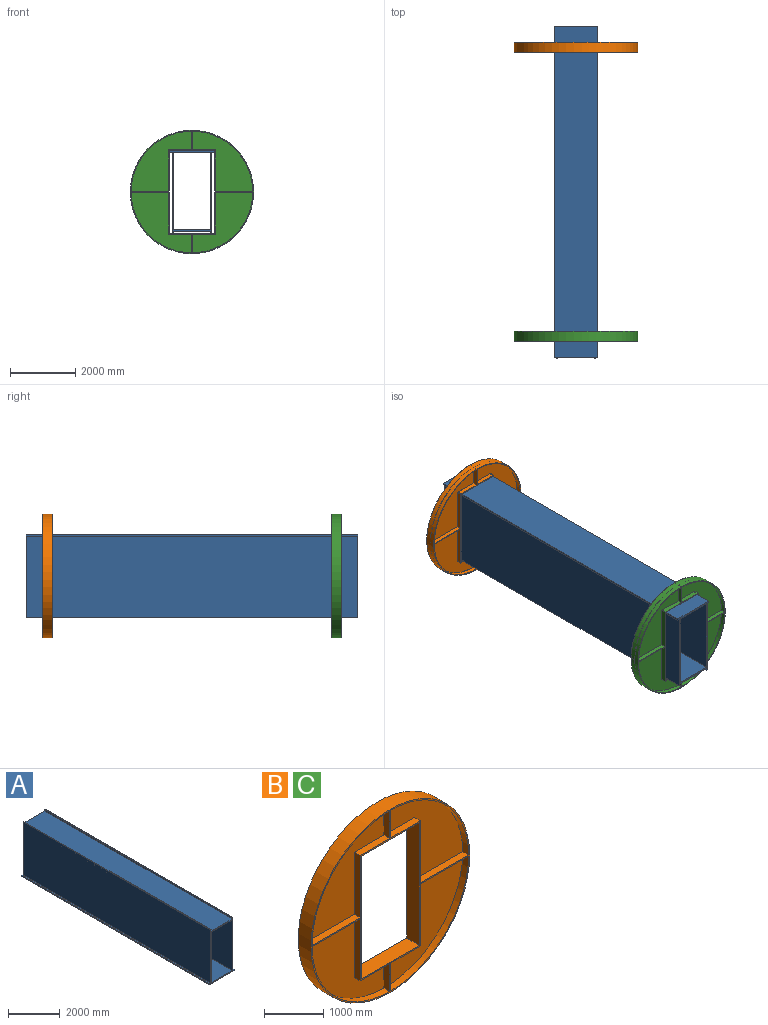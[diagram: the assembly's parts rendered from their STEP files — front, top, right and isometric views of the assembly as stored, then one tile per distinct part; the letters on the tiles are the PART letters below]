
ASSEMBLY  parts=3 mates=2
PART A: 18 faces, bbox 1346.2x10207.6x2552.7 mm
  f0: plane 10207.63x63.5mm, normal (0,0,1), area 648184.2mm2, adj f1,f15,f16,f17
  f1: plane 10207.63x2501.9mm, normal (1,0,0), area 25538457mm2, adj f0,f2,f16,f17
  f2: plane 10207.63x38.1mm, normal (0,0,1), area 388910.5mm2, adj f1,f3,f16,f17
  f3: plane 10207.63x63.5mm, normal (-1,0,0), area 648184.2mm2, adj f2,f4,f16,f17
  f4: plane 10207.63x1143mm, normal (0,0,1), area 11667315.4mm2, adj f3,f5,f16,f17
  f5: plane 10207.63x63.5mm, normal (1,0,0), area 648184.2mm2, adj f4,f6,f16,f17
  f6: plane 10207.63x38.1mm, normal (0,0,1), area 388910.5mm2, adj f5,f7,f16,f17
  f7: plane 10207.63x2501.9mm, normal (-1,0,0), area 25538457mm2, adj f6,f8,f16,f17
  f8: plane 10207.63x63.5mm, normal (0,0,1), area 648184.2mm2, adj f7,f9,f16,f17
  f9: plane 10207.63x50.8mm, normal (-1,0,0), area 518547.3mm2, adj f8,f10,f16,f17
  f10: plane 10207.63x1346.2mm, normal (0,0,-1), area 13741504.8mm2, adj f9,f15,f16,f17
  f11: plane 10207.63x2387.6mm, normal (-1,0,0), area 24371725.4mm2, adj f12,f14,f16,f17
  f12: plane 10207.63x1143mm, normal (0,0,1), area 11667315.4mm2, adj f11,f13,f16,f17
  f13: plane 10207.63x2387.6mm, normal (1,0,0), area 24371725.4mm2, adj f12,f14,f16,f17
  f14: plane 10207.63x1143mm, normal (0,0,-1), area 11667315.4mm2, adj f11,f13,f16,f17
  f15: plane 10207.63x50.8mm, normal (1,0,0), area 518547.3mm2, adj f0,f10,f16,f17
  f16: plane 2552.7x1346.2mm, normal (0,-1,0), area 317096.1mm2, adj f0,f1,f2,f3,f4,f5,f6,f7
  f17: plane 2552.7x1346.2mm, normal (0,1,0), area 317096.1mm2, adj f0,f1,f2,f3,f4,f5,f6,f7
PART B: 59 faces, bbox 3794.3x304.8x3794.3 mm
  f0: plane 1871.68x1859.03mm, normal (0,1,0), area 1802159.4mm2, adj f1,f9,f11,f48,f57
  f1: plane 1284.17x139.7mm, normal (1,0,0), area 179399mm2, adj f0,f11,f23,f57
  f2: cylinder r=1871.73mm len=1871.68mm, axis (0,1,0), area 407192.8mm2, adj f8,f23,f52,f53,f58
  f3: plane 1858.98x1858.98mm, normal (0,1,0), area 1794859.1mm2, adj f6,f10,f36,f51,f56
  f4: plane 1284.17x139.7mm, normal (-1,0,0), area 179399mm2, adj f7,f23,f35,f55
  f5: cylinder r=1871.73mm len=1884.26mm, axis (0,1,0), area 407177mm2, adj f7,f23,f47,f50,f55
  f6: plane 733.35x139.7mm, normal (0,0,-1), area 98911.6mm2, adj f3,f23,f36,f51,f54
  f7: plane 1858.98x1858.98mm, normal (0,1,0), area 1794859.1mm2, adj f4,f5,f35,f47,f55
  f8: plane 1871.68x1859.03mm, normal (0,1,0), area 1802159.4mm2, adj f2,f37,f38,f52,f58
  f9: cylinder r=1871.73mm len=1871.68mm, axis (0,1,0), area 407192.8mm2, adj f0,f23,f48,f49,f57
  f10: cylinder r=1871.73mm len=1884.26mm, axis (0,1,0), area 407177mm2, adj f3,f23,f51,f54,f56
  f11: plane 720.78x139.7mm, normal (0,0,1), area 98927.4mm2, adj f0,f1,f23,f48,f49
  f12: plane 1858.98x1858.98mm, normal (0,-1,0), area 1794859mm2, adj f13,f20,f33,f41,f46
  f13: plane 708.08x139.7mm, normal (0,0,-1), area 98918.2mm2, adj f12,f29,f33,f46
  f14: cylinder r=1871.73mm len=1858.98mm, axis (0,-1,0), area 407183.6mm2, adj f22,f29,f39,f45
  f15: plane 1858.98x1858.98mm, normal (0,-1,0), area 1794859mm2, adj f21,f30,f34,f40,f43
  f16: plane 708.08x139.7mm, normal (0,0,1), area 98918.2mm2, adj f18,f19,f29,f44
  f17: cylinder r=1871.73mm len=1858.98mm, axis (0,-1,0), area 407183.6mm2, adj f18,f29,f42,f44
  f18: plane 1858.98x1858.98mm, normal (0,-1,0), area 1794859mm2, adj f16,f17,f19,f42,f44
  f19: plane 1284.17x139.7mm, normal (-1,0,0), area 179399mm2, adj f16,f18,f29,f42
  f20: cylinder r=1871.73mm len=1858.98mm, axis (0,-1,0), area 407183.6mm2, adj f12,f29,f41,f46
  f21: plane 1284.17x139.7mm, normal (1,0,0), area 179399mm2, adj f15,f29,f30,f40
  f22: plane 1858.98x1858.98mm, normal (0,-1,0), area 1794859mm2, adj f14,f31,f32,f39,f45
  f23: plane 3794.25x3794.25mm, normal (0,1,0), area 561621.1mm2, adj f1,f2,f4,f5,f6,f9,f10,f11
  f24: plane 1390.75x304.8mm, normal (0,0,-1), area 423901.1mm2, adj f23,f25,f27,f29
  f25: plane 2542.95x304.8mm, normal (-1,0,0), area 775090.1mm2, adj f23,f24,f26,f29
  f26: plane 1390.75x304.8mm, normal (0,0,1), area 423901.1mm2, adj f23,f25,f27,f29
  f27: plane 2542.95x304.8mm, normal (1,0,0), area 775090.1mm2, adj f23,f24,f26,f29
  f28: cylinder r=1897.13mm len=3794.25mm, axis (0,1,0), area 3633214.2mm2, adj f23,f29
  f29: plane 3794.25x3794.25mm, normal (0,-1,0), area 590822.9mm2, adj f13,f14,f16,f17,f19,f20,f21,f24
  f30: plane 708.08x139.7mm, normal (0,0,1), area 98918.2mm2, adj f15,f21,f29,f43
  f31: plane 1284.17x139.7mm, normal (1,0,0), area 179399mm2, adj f22,f29,f32,f39
  f32: plane 708.08x139.7mm, normal (0,0,-1), area 98918.2mm2, adj f22,f29,f31,f45
  f33: plane 1284.17x139.7mm, normal (-1,0,0), area 179399mm2, adj f12,f13,f29,f41
  f34: cylinder r=1871.73mm len=1858.98mm, axis (0,-1,0), area 407183.6mm2, adj f15,f29,f40,f43
  f35: plane 733.35x139.7mm, normal (0,0,1), area 98911.6mm2, adj f4,f7,f23,f47,f50
  f36: plane 1284.17x139.7mm, normal (-1,0,0), area 179399mm2, adj f3,f6,f23,f56
  f37: plane 720.78x139.7mm, normal (0,0,-1), area 98927.4mm2, adj f8,f23,f38,f52,f53
  f38: plane 1284.17x139.7mm, normal (1,0,0), area 179399mm2, adj f8,f23,f37,f58
  f39: plane 1150.91x139.7mm, normal (0,0,-1), area 160781.7mm2, adj f14,f22,f29,f31
  f40: plane 1150.91x139.7mm, normal (0,0,1), area 160781.7mm2, adj f15,f21,f29,f34
  f41: plane 1150.91x139.7mm, normal (0,0,-1), area 160781.7mm2, adj f12,f20,f29,f33
  f42: plane 1150.91x139.7mm, normal (0,0,1), area 160781.7mm2, adj f17,f18,f19,f29
  f43: plane 574.81x139.7mm, normal (1,0,0), area 80300.9mm2, adj f15,f29,f30,f34
  f44: plane 574.81x139.7mm, normal (-1,0,0), area 80300.9mm2, adj f16,f17,f18,f29
  f45: plane 574.81x139.7mm, normal (1,0,0), area 80300.9mm2, adj f14,f22,f29,f32
  f46: plane 574.81x139.7mm, normal (-1,0,0), area 80300.9mm2, adj f12,f13,f20,f29
  f47: plane 574.81x139.54mm, normal (-1,0,0), area 80209.6mm2, adj f5,f7,f35,f50
  f48: plane 574.85x12.7mm, normal (0.01,-1,0), area 7300.4mm2, adj f0,f9,f11,f49
  f49: plane 574.81x139.62mm, normal (1,0,0), area 80255.4mm2, adj f9,f11,f48,f50
  f50: plane 574.85x25.4mm, normal (-0.01,1,0), area 14600.9mm2, adj f5,f35,f47,f49
  f51: plane 574.81x139.54mm, normal (-1,0,0), area 80209.6mm2, adj f3,f6,f10,f54
  f52: plane 574.85x12.7mm, normal (0.01,-1,0), area 7300.4mm2, adj f2,f8,f37,f53
  f53: plane 574.81x139.62mm, normal (1,0,0), area 80255.4mm2, adj f2,f37,f52,f54
  f54: plane 574.85x25.4mm, normal (-0.01,1,0), area 14600.9mm2, adj f6,f10,f51,f53
  f55: plane 1150.91x139.7mm, normal (0,0,1), area 160781.7mm2, adj f4,f5,f7,f23
  f56: plane 1150.91x139.7mm, normal (0,0,-1), area 160781.7mm2, adj f3,f10,f23,f36
  f57: plane 1150.91x139.7mm, normal (0,0,1), area 160781.7mm2, adj f0,f1,f9,f23
  f58: plane 1150.91x139.7mm, normal (0,0,-1), area 160781.7mm2, adj f2,f8,f23,f38
PART C: same geometry as B
PLACE A rot(axis=(0,1,0),180deg) t=(-1288.74,7201.97,-1155.72)mm
PLACE B t=(-1288.74,6693.97,-2401.8)mm
PLACE C t=(-1288.74,-2192.85,-2401.8)mm
MATE fastened A.f10 <-> C.f24  axis (0,0,1) through (-1288.74,-3005.65,-1130.32)mm
MATE fastened B.f24 <-> A.f10  axis (0,0,-1) through (-1288.74,6693.97,-1130.32)mm
